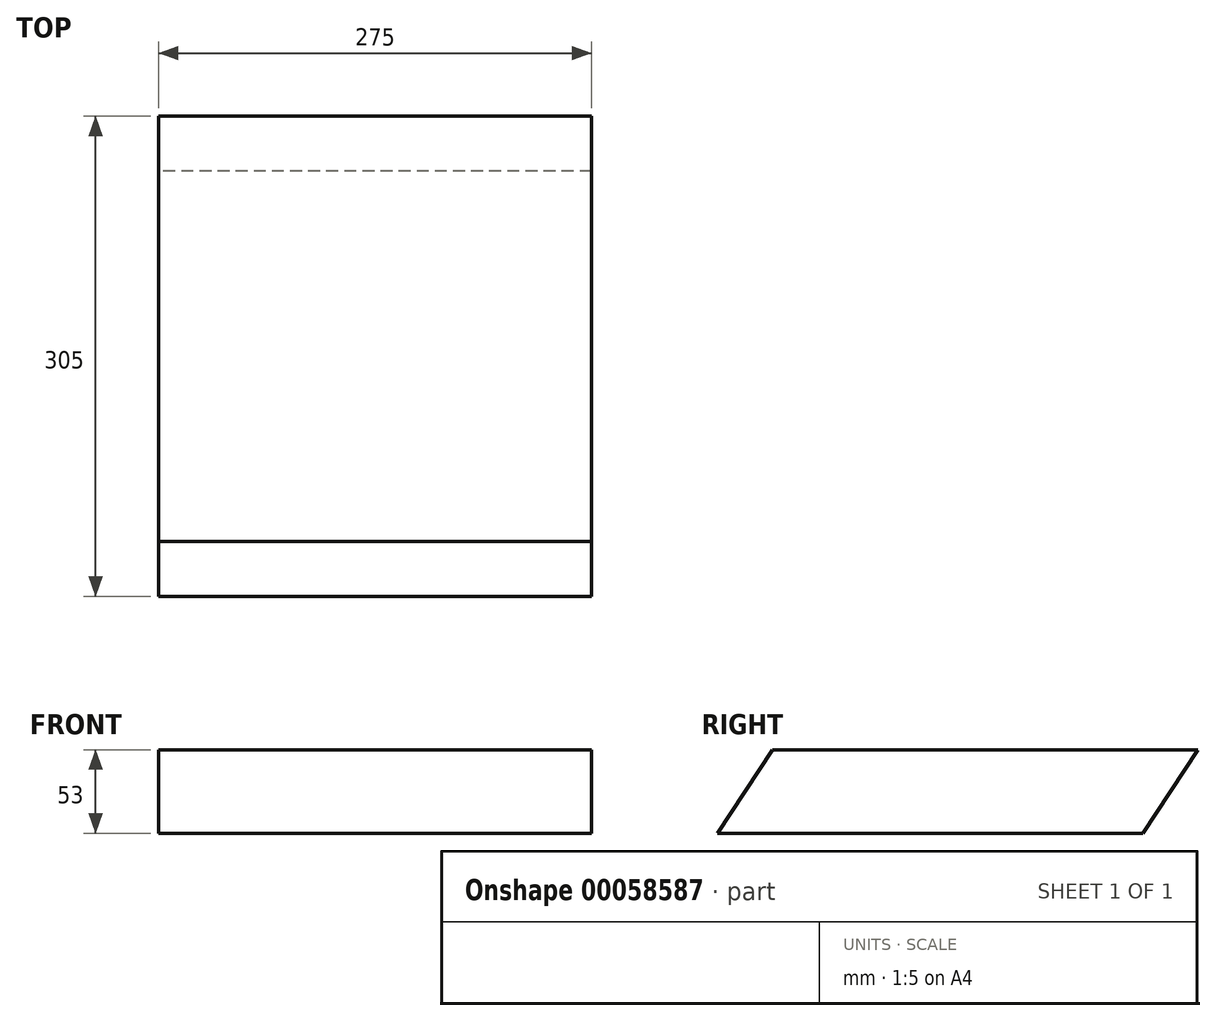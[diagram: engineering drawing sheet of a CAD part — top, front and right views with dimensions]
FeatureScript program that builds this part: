
annotation { "Feature Type Name" : "Feature", "Feature Type Description" : "" }
export const myFeature = defineFeature(function(context is Context, id is Id, definition is map)
    precondition{}
    {
        {
            var Q0;
            Q0=qCreatedBy(makeId("Right.planeOp"),FACE);
            var sketch = newSketch(context, id + "F0", { "sketchPlane" : qUnion([Q0])});
            skLineSegment(sketch, "E0", {"start": v(-111.9, 12.25) * mm, "end": v(158.1, 12.25) * mm});
            skLineSegment(sketch, "E1", {"start": v(158.1, 12.25) * mm, "end": v(123.1, -40.75) * mm});
            skLineSegment(sketch, "E2", {"start": v(123.1, -40.75) * mm, "end": v(-146.9, -40.75) * mm});
            skLineSegment(sketch, "E3", {"start": v(-146.9, -40.75) * mm, "end": v(-111.9, 12.25) * mm});
            skSolve(sketch);
        }
        {
            var Q0;
            Q0 = qSketchRegion(id + "F0", true);
            extrude(context, id + "F1", {"entities" : qUnion([Q0]), "depth" : 137.5 * mm, "hasSecondDirection" : true, "secondDirectionOppositeDirection" : true, "secondDirectionDepth" : 137.5 * mm});
        }
    });
